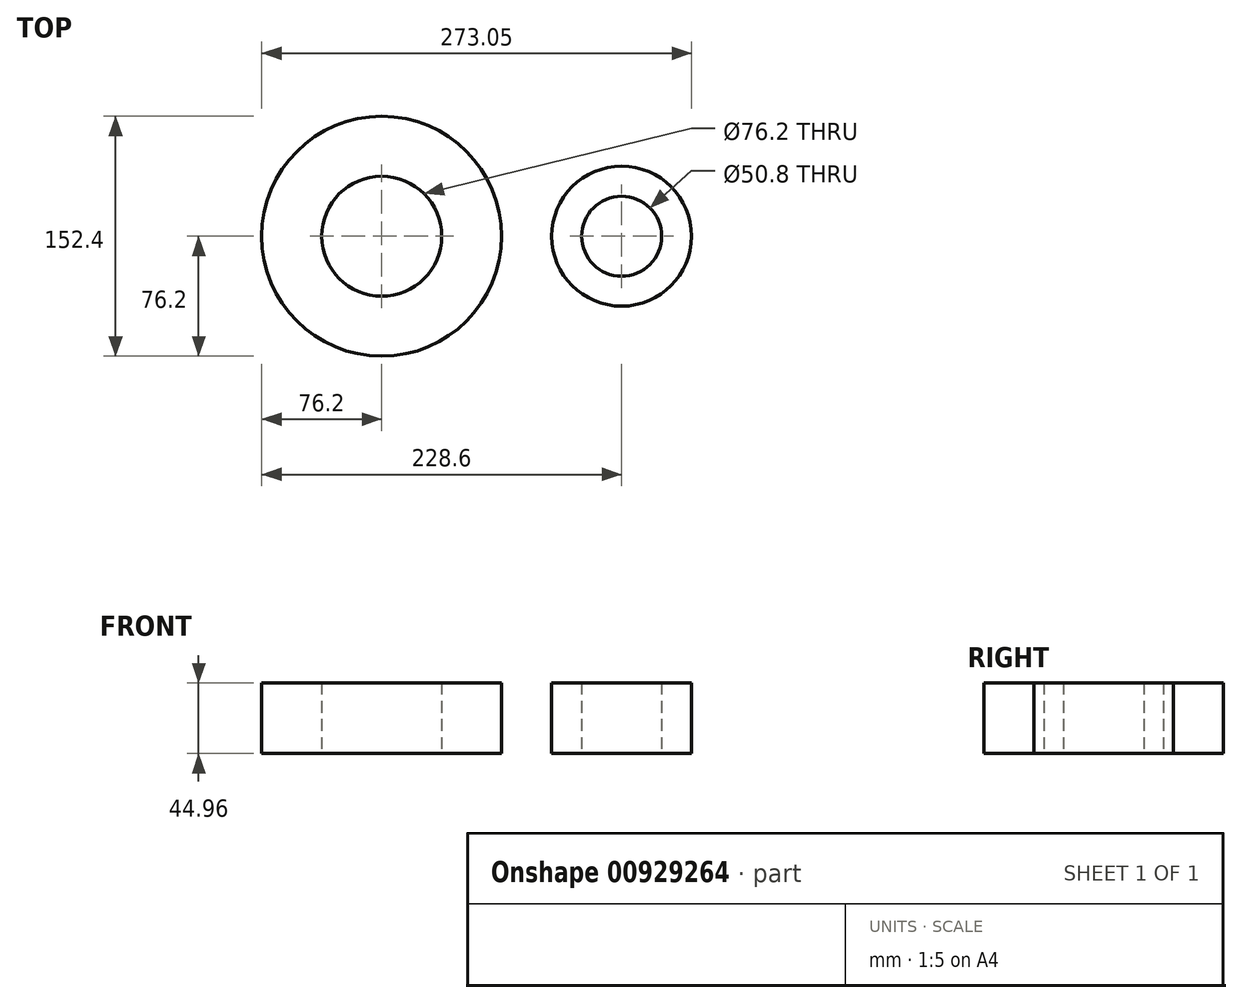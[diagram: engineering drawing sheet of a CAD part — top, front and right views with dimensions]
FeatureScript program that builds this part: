
annotation { "Feature Type Name" : "Feature", "Feature Type Description" : "" }
export const myFeature = defineFeature(function(context is Context, id is Id, definition is map)
    precondition{}
    {
        {
            var Q0;
            Q0=qCreatedBy(makeId("Top.planeOp"),FACE);
            var sketch = newSketch(context, id + "F0", { "sketchPlane" : qUnion([Q0])});
            skCircle(sketch, "E0", {"center": v(0, 0) * mm, "radius": 76.2 * mm});
            skCircle(sketch, "E1", {"center": v(152.4, 0) * mm, "radius": 44.45 * mm});
            skLineSegment(sketch, "E2", {"start": v(15.87, 74.53) * mm, "end": v(156.21, 44.63) * mm});
            skLineSegment(sketch, "E3", {"start": v(15.88, -74.53) * mm, "end": v(161.66, -43.47) * mm});
            skCircle(sketch, "E4", {"center": v(0, 0) * mm, "radius": 38.1 * mm});
            skCircle(sketch, "E5", {"center": v(152.4, 0) * mm, "radius": 25.4 * mm});
            skSolve(sketch);
        }
        {
            var Q0;
            Q0 = qSketchRegion(id + "F0", true);
            extrude(context, id + "F1", {"entities" : qUnion([Q0]), "depth" : 44.96 * mm, "offsetDistance" : 25.4 * mm});
        }
    });
